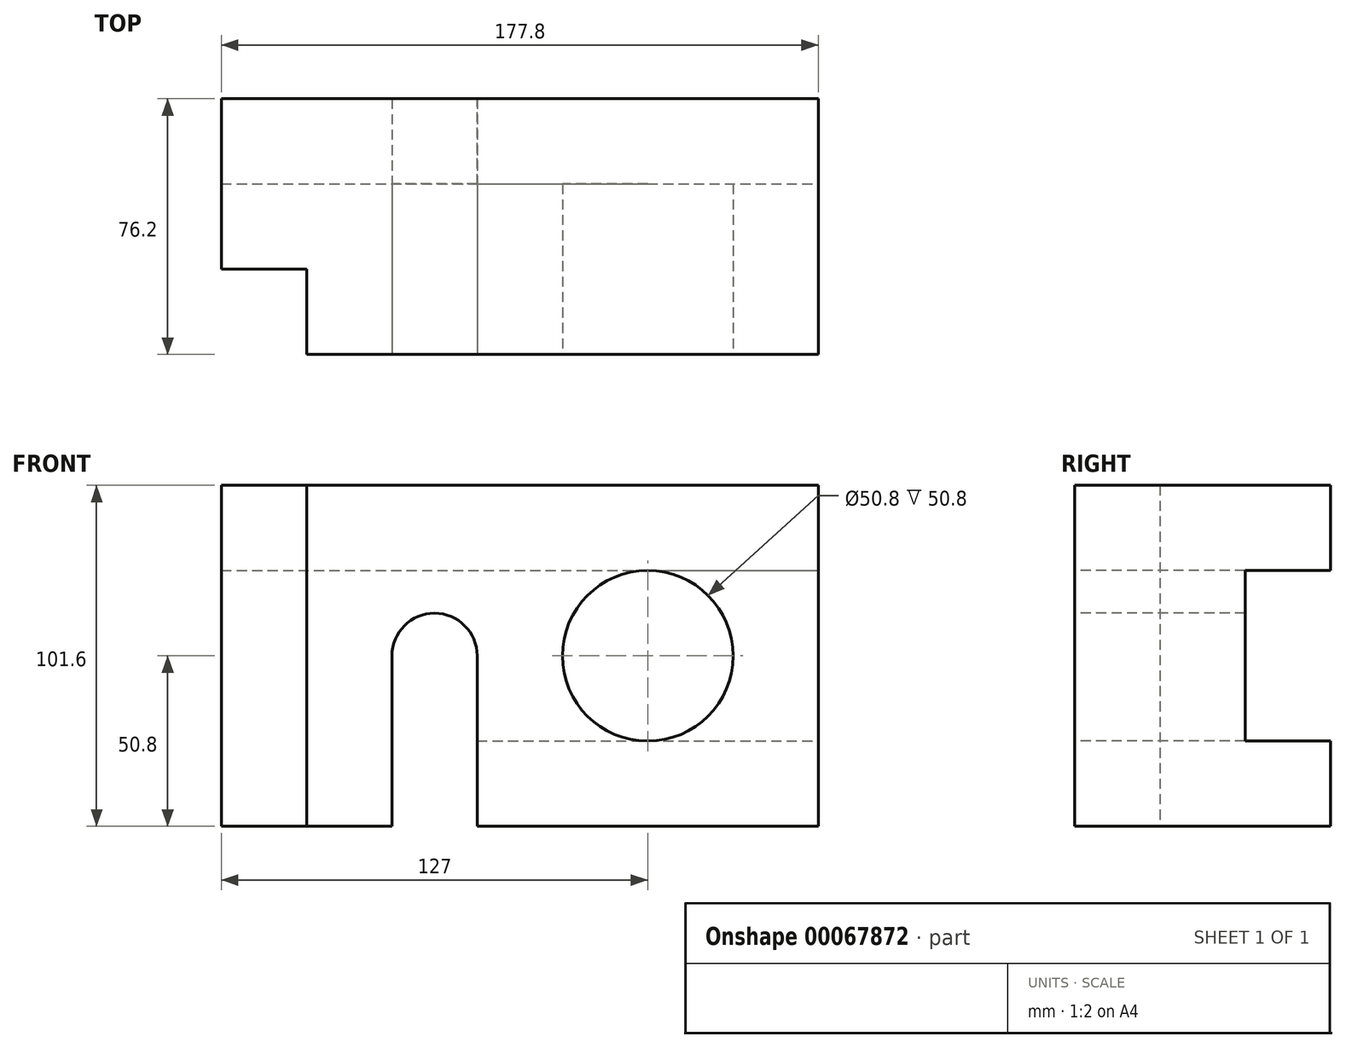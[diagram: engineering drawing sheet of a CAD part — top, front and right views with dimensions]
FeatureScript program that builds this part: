
annotation { "Feature Type Name" : "Feature", "Feature Type Description" : "" }
export const myFeature = defineFeature(function(context is Context, id is Id, definition is map)
    precondition{}
    {
        {
            var Q0;
            Q0=qCreatedBy(makeId("Top.planeOp"),FACE);
            var sketch = newSketch(context, id + "F0", { "sketchPlane" : qUnion([Q0])});
            skLineSegment(sketch, "E0", {"start": v(0, 0) * mm, "end": v(0, 25.4) * mm});
            skLineSegment(sketch, "E1", {"start": v(0, 25.4) * mm, "end": v(-25.4, 25.4) * mm});
            skLineSegment(sketch, "E2", {"start": v(-25.4, 25.4) * mm, "end": v(-25.4, 76.2) * mm});
            skLineSegment(sketch, "E3", {"start": v(-25.4, 76.2) * mm, "end": v(152.4, 76.2) * mm});
            skLineSegment(sketch, "E4", {"start": v(152.4, 76.2) * mm, "end": v(152.4, 0) * mm});
            skLineSegment(sketch, "E5", {"start": v(152.4, 0) * mm, "end": v(0, 0) * mm});
            skSolve(sketch);
        }
        {
            var Q0;
            Q0=makeQuery(id+"F0.imprint","IMPRINT",FACE,{"disambiguationData":[TD([[makeQuery(id+"F0.imprint","IMPRINT",EDGE,{"derivedFrom":sQuery(id+"F0.wireOp",EDGE,"E0")}),-1.0]])]});
            extrude(context, id + "F1", {"entities" : qUnion([Q0]), "depth" : 101.6 * mm});
        }
        {
            var Q0;
            Q0=makeQuery(id+"F1.opExtrude","SWEPT_FACE",FACE,{"disambiguationData":[OSD([sQuery(id+"F0.wireOp",EDGE,"E5")])]});
            var sketch = newSketch(context, id + "F2", { "sketchPlane" : qUnion([Q0])});
            skLineSegment(sketch, "E6", {"start": v(25.4, 0) * mm, "end": v(25.4, 50.8) * mm});
            skArc(sketch, "E7", {"start": v(25.4, 50.8) * mm, "mid": v(38.1, 63.5) * mm, "end": v(50.8, 50.8) * mm});
            skLineSegment(sketch, "E8", {"start": v(50.8, 50.8) * mm, "end": v(50.8, 0) * mm});
            skLineSegment(sketch, "E9", {"start": v(25.4, 0) * mm, "end": v(50.8, 0) * mm});
            skCircle(sketch, "E10", {"center": v(101.6, 50.8) * mm, "radius": 25.4 * mm});
            skSolve(sketch);
        }
        {
            var Q0;
            Q0=makeQuery(id+"F2.imprint","IMPRINT",FACE,{"disambiguationData":[TD([[makeQuery(id+"F2.imprint","IMPRINT",EDGE,{"derivedFrom":sQuery(id+"F2.wireOp",EDGE,"E6")}),-1.0]])]});
            var Q1;
            Q1=makeQuery(id+"F2.imprint","IMPRINT",FACE,{"disambiguationData":[TD([[makeQuery(id+"F2.imprint","IMPRINT",EDGE,{"derivedFrom":sQuery(id+"F2.wireOp",EDGE,"E10")}),1.0]])]});
            extrude(context, id + "F3", {"entities" : qUnion([Q0, Q1]), "operationType" : NewBodyOperationType.REMOVE, "endBound" : BoundingType.THROUGH_ALL, "oppositeDirection" : true, "depth" : 25.4 * mm});
        }
        {
            var Q0;
            Q0=makeQuery(id+"F1.opExtrude","SWEPT_FACE",FACE,{"disambiguationData":[OSD([sQuery(id+"F0.wireOp",EDGE,"E4")])]});
            var sketch = newSketch(context, id + "F4", { "sketchPlane" : qUnion([Q0])});
            skLineSegment(sketch, "E11.bottom", {"start": v(76.2, 76.2) * mm, "end": v(50.8, 76.2) * mm});
            skLineSegment(sketch, "E11.top", {"start": v(76.2, 25.4) * mm, "end": v(50.8, 25.4) * mm});
            skLineSegment(sketch, "E11.left", {"start": v(76.2, 76.2) * mm, "end": v(76.2, 25.4) * mm});
            skLineSegment(sketch, "E11.right", {"start": v(50.8, 76.2) * mm, "end": v(50.8, 25.4) * mm});
            skSolve(sketch);
        }
        {
            var Q0;
            Q0=makeQuery(id+"F4.imprint","IMPRINT",FACE,{"disambiguationData":[TD([[makeQuery(id+"F4.imprint","IMPRINT",EDGE,{"derivedFrom":sQuery(id+"F4.wireOp",EDGE,"E11.bottom")}),1.0]])]});
            extrude(context, id + "F5", {"entities" : qUnion([Q0]), "operationType" : NewBodyOperationType.REMOVE, "endBound" : BoundingType.THROUGH_ALL, "oppositeDirection" : true, "depth" : 25.4 * mm});
        }
    });
